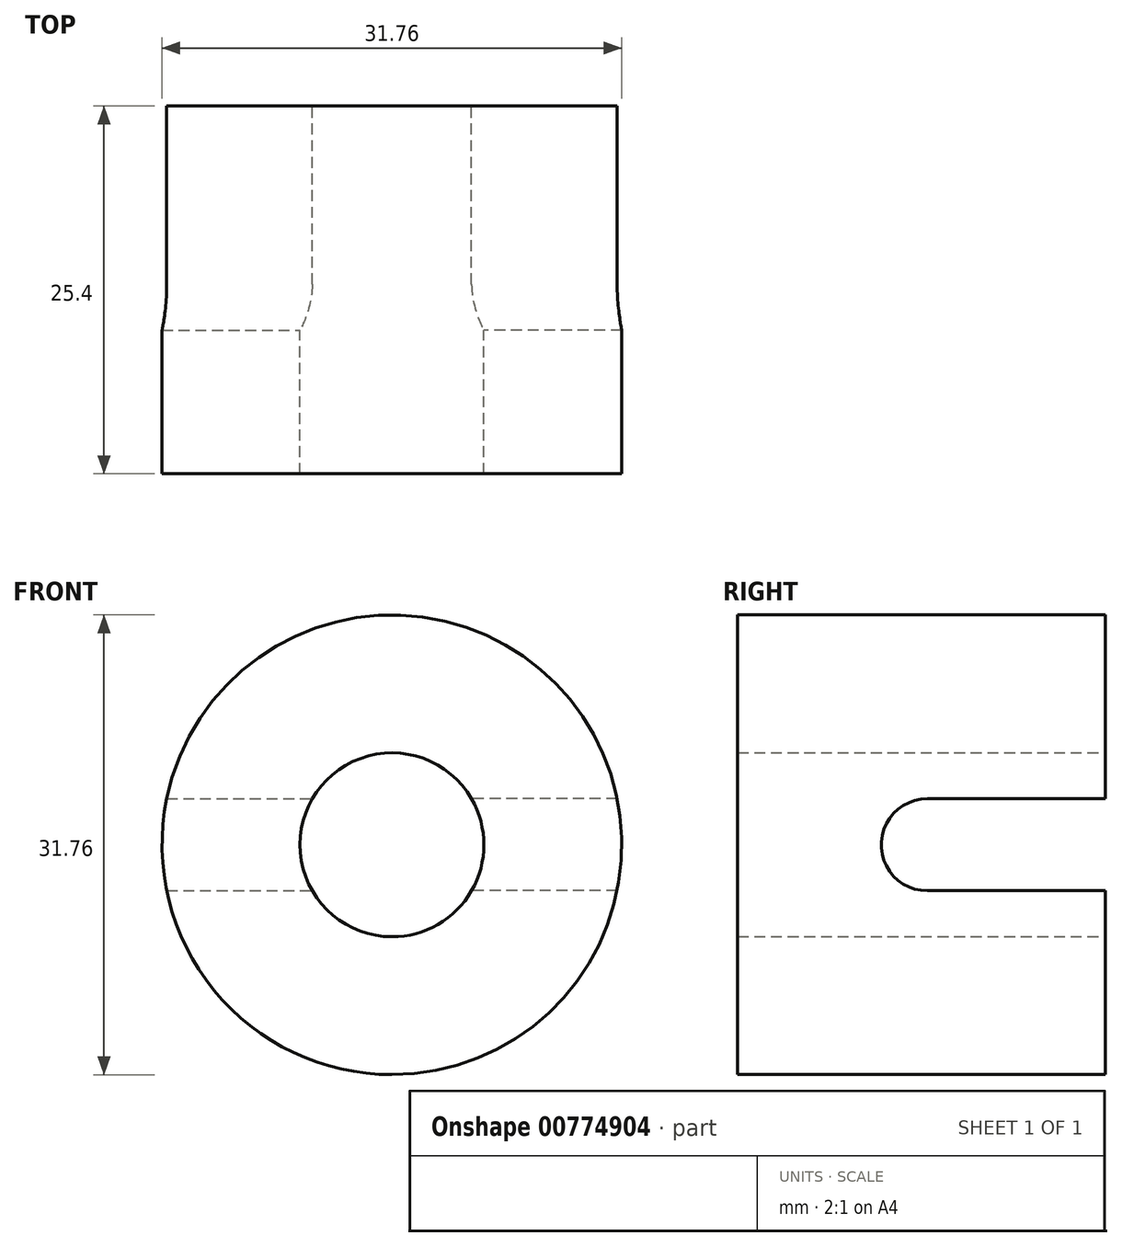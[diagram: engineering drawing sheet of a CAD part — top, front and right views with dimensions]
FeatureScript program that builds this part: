
annotation { "Feature Type Name" : "Feature", "Feature Type Description" : "" }
export const myFeature = defineFeature(function(context is Context, id is Id, definition is map)
    precondition{}
    {
        {
            var Q0;
            Q0=qCreatedBy(makeId("Front.planeOp"),FACE);
            var sketch = newSketch(context, id + "F0", { "sketchPlane" : qUnion([Q0])});
            skCircle(sketch, "E0", {"center": v(0, 0) * mm, "radius": 15.88 * mm});
            skCircle(sketch, "E1", {"center": v(0, 0) * mm, "radius": 6.35 * mm});
            skSolve(sketch);
        }
        {
            var Q0;
            Q0=makeQuery(id+"F0.imprint","IMPRINT",FACE,{"disambiguationData":[TD([[makeQuery(id+"F0.imprint","IMPRINT",EDGE,{"derivedFrom":sQuery(id+"F0.wireOp",EDGE,"E0")}),1.0]])]});
            extrude(context, id + "F1", {"entities" : qUnion([Q0]), "depth" : 25.4 * mm, "offsetDistance" : 25.4 * mm});
        }
        {
            var Q0;
            Q0=qCreatedBy(makeId("Right.planeOp"),FACE);
            var sketch = newSketch(context, id + "F2", { "sketchPlane" : qUnion([Q0])});
            skCircle(sketch, "E2", {"center": v(0, 0) * mm, "radius": 3.18 * mm});
            skSolve(sketch);
        }
        {
            var Q0;
            Q0 = qSketchRegion(id + "F2", true);
            extrude(context, id + "F3", {"entities" : qUnion([Q0]), "operationType" : NewBodyOperationType.REMOVE, "oppositeDirection" : true, "depth" : 25.4 * mm, "offsetDistance" : 25.4 * mm});
        }
        {
            var Q0;
            Q0=qCreatedBy(makeId("Right.planeOp"),FACE);
            var sketch = newSketch(context, id + "F4", { "sketchPlane" : qUnion([Q0])});
            skArc(sketch, "E3", {"start": v(-12.31, 3.18) * mm, "mid": v(-15.49, 0) * mm, "end": v(-12.31, -3.18) * mm});
            skPoint(sketch, "E4.center.orphan", {"position": v(0, 0) * mm});
            skLineSegment(sketch, "E5", {"start": v(-12.31, 3.17) * mm, "end": v(0, 3.17) * mm});
            skLineSegment(sketch, "E6", {"start": v(0, 3.17) * mm, "end": v(0, 3.17) * mm});
            skLineSegment(sketch, "E7", {"start": v(-12.31, -3.17) * mm, "end": v(0, -3.17) * mm});
            skLineSegment(sketch, "E8", {"start": v(0, 3.17) * mm, "end": v(0, -3.17) * mm});
            skSolve(sketch);
        }
        {
            var Q0;
            Q0 = qSketchRegion(id + "F4", true);
            extrude(context, id + "F5", {"entities" : qUnion([Q0]), "operationType" : NewBodyOperationType.REMOVE, "depth" : 25.4 * mm, "offsetDistance" : 25.4 * mm});
        }
        {
            var Q0;
            Q0 = qSketchRegion(id + "F4", true);
            extrude(context, id + "F6", {"entities" : qUnion([Q0]), "operationType" : NewBodyOperationType.REMOVE, "oppositeDirection" : true, "depth" : 25.4 * mm, "offsetDistance" : 25.4 * mm});
        }
    });
